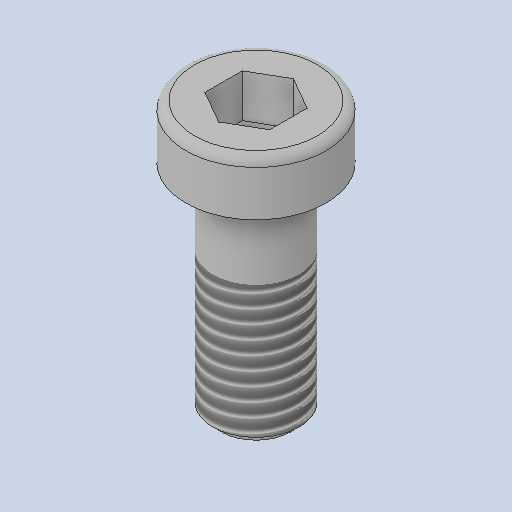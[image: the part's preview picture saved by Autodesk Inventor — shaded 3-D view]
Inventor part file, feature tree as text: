
AUTODESK INVENTOR PART (.ipt)
format: ipt  version: 2023 (Build 270158000, 158)  size: 171,520 bytes
history: native  units: mm
features: other x7, sketch x2, revolve x1, thread x1, extrude x1
ambient origin geometry x8: Origin, YZ Plane, XZ Plane, XY Plane, X Axis, Y Axis, Z Axis, Center Point
bodies: Solid1 (feature_tree)
feature tree (12):
  revolve  "Revolution1"  [1 undecoded]
  thread  "Thread1"  [1 undecoded]
  extrude  "Extrusion1"  [1 undecoded]
  other  "p1_XY"
  other  "p1_YZ"
  other  "p1_ZX"
  other  "p1_X"
  other  "p1_Y"
  other  "p1_Z"
  other  "p1_Center"
  sketch  "Sketch_1"  dims[d0=360.0deg d1=12.233mm d2=0.0mm d3=4.0mm d4=0.0mm]
  sketch  "Sketch_2"  dims[d5=0.0mm]
note: 3 required parameter values undecoded (feature->parameter linkage not recoverable at this tier; creation-order binding heuristic only, values carry confidence <= 0.55)